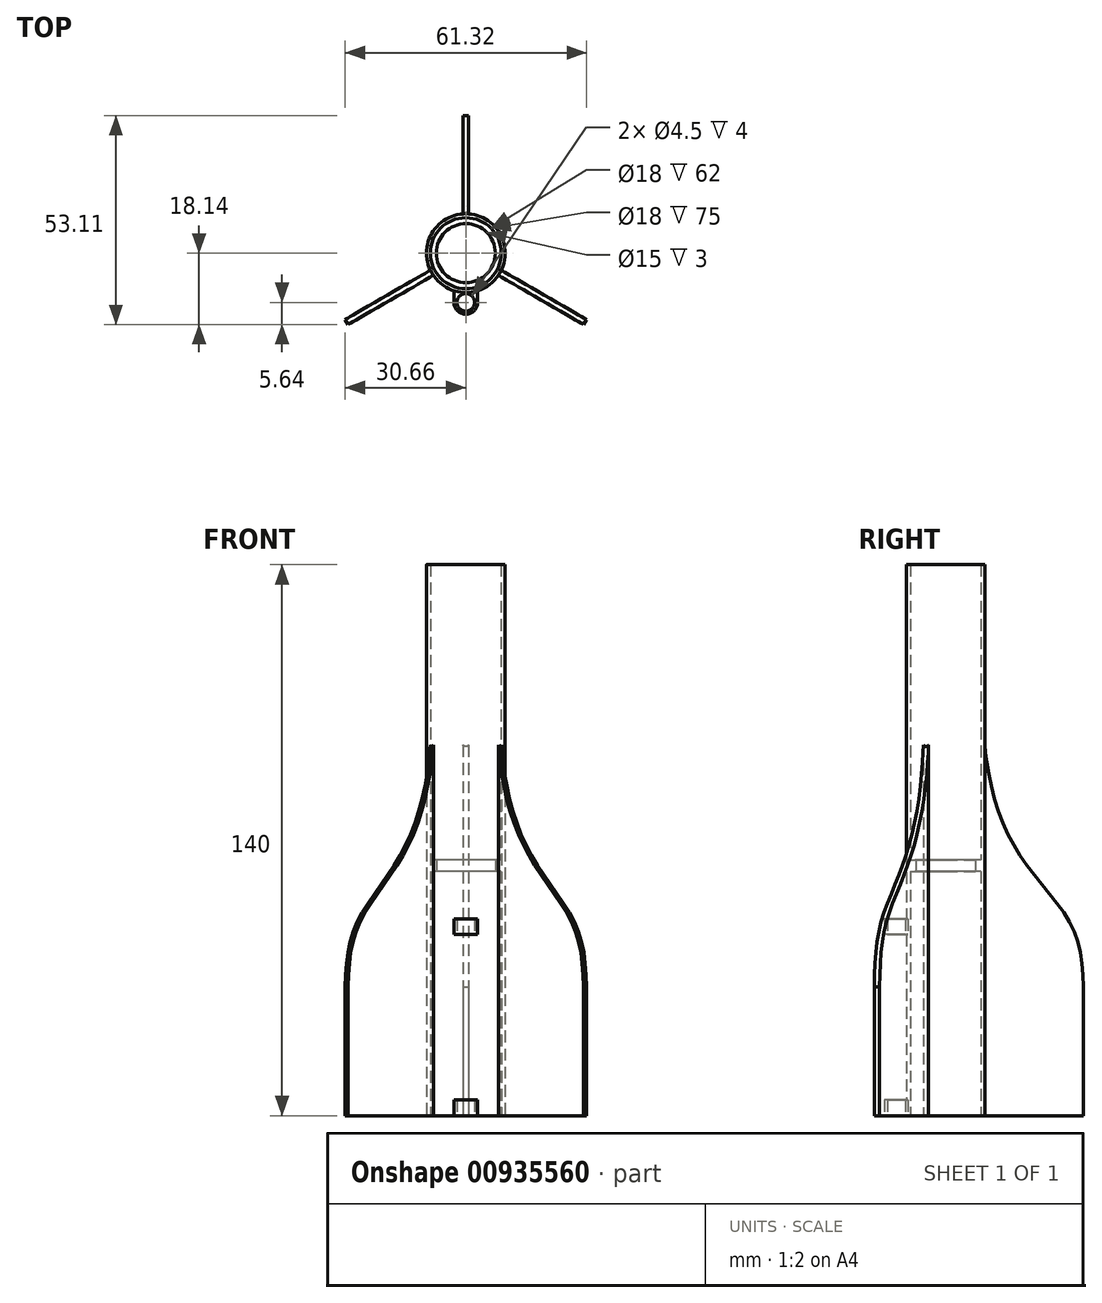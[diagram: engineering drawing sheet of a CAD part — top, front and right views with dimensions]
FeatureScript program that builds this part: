
annotation { "Feature Type Name" : "Feature", "Feature Type Description" : "" }
export const myFeature = defineFeature(function(context is Context, id is Id, definition is map)
    precondition{}
    {
        {
            var Q0;
            Q0=qCreatedBy(makeId("Top.planeOp"),FACE);
            var sketch = newSketch(context, id + "F0", { "sketchPlane" : qUnion([Q0])});
            skCircle(sketch, "E0", {"center": v(0, 0) * mm, "radius": 9 * mm});
            skCircle(sketch, "E1", {"center": v(0, -12.5) * mm, "radius": 2.25 * mm});
            skArc(sketch, "E2", {"start": v(-1.48, -9.89) * mm, "mid": v(0, -15.5) * mm, "end": v(1.48, -9.9) * mm});
            skLineSegment(sketch, "E3", {"start": v(3, -12.5) * mm, "end": v(3, -9.54) * mm});
            skLineSegment(sketch, "E4", {"start": v(-3, -12.5) * mm, "end": v(-3, -9.54) * mm});
            skLineSegment(sketch, "E5.top", {"start": v(0.75, 34.97) * mm, "end": v(-0.75, 34.97) * mm});
            skLineSegment(sketch, "E5.left", {"start": v(0.75, 9.97) * mm, "end": v(0.75, 34.97) * mm});
            skLineSegment(sketch, "E5.right", {"start": v(-0.75, 9.97) * mm, "end": v(-0.75, 34.97) * mm});
            skPoint(sketch, "E5.middle", {"position": v(0, 22.47) * mm});
            skCircle(sketch, "E6", {"center": v(0, 0) * mm, "radius": 10 * mm});
            skCircle(sketch, "E7", {"center": v(0, 0) * mm, "radius": 7.5 * mm});
            skSolve(sketch);
        }
        {
            var Q0;
            Q0=makeQuery(id+"F0.imprint","IMPRINT",FACE,{"disambiguationData":[TD([[makeQuery(id+"F0.imprint","IMPRINT",EDGE,{"derivedFrom":sQuery(id+"F0.wireOp",EDGE,"E0")}),-1.0]])]});
            var Q1;
            {var subQ0=sQuery(id+"F0.wireOp",EDGE,"ZZ5YX0io-akKa-NGHC-uEbq-0SfljBpc04vF");Q1=makeQuery(id+"F0.imprint","IMPRINT",FACE,{"disambiguationData":[TD([[makeQuery(id+"F0.imprint","IMPRINT",EDGE,{"derivedFrom":subQ0}),1.0]])]});}
            extrude(context, id + "F1", {"entities" : qUnion([Q0, Q1]), "depth" : 140 * mm, "offsetDistance" : 25 * mm});
        }
        {
            var Q0;
            Q0=makeQuery(id+"F0.imprint","IMPRINT",FACE,{"disambiguationData":[TD([[makeQuery(id+"F0.imprint","IMPRINT",EDGE,{"derivedFrom":sQuery(id+"F0.wireOp",EDGE,"E5.top")}),1.0]])]});
            extrude(context, id + "F2", {"entities" : qUnion([Q0]), "operationType" : NewBodyOperationType.ADD, "depth" : 100 * mm, "offsetDistance" : 25 * mm});
        }
        {
            var Q0;
            Q0=makeQuery(id+"F2.opExtrude","SWEPT_FACE",FACE,{"disambiguationData":[OSD([sQuery(id+"F0.wireOp",EDGE,"E5.left")])]});
            var sketch = newSketch(context, id + "F3", { "sketchPlane" : qUnion([Q0])});
            skFitSpline(sketch, "E8", {"points": [v(9.97, 100) * mm, v(9.97, 94.16) * mm, v(12.9, 78.8) * mm, v(21.82, 61.99) * mm, v(32.08, 48.03) * mm, v(34.97, 32.7) * mm, v(34.97, 12.12) * mm, v(34.97, 0) * mm], "startDerivative": vector(0, -120.5) * mm, "endDerivative": vector(0, -110.6) * mm});
            skSolve(sketch);
        }
        {
            var Q0;
            {var subQ1=sQuery(id+"F0.wireOp",EDGE,"E5.left");var subQ2=makeQuery(id+"F2.opExtrude","CAP_EDGE",EDGE,{"disambiguationData":[OSD([subQ1])],"isStart":false});Q0=makeQuery(id+"F3.imprint","IMPRINT",FACE,{"disambiguationData":[TD([[makeQuery(id+"F3.imprint","IMPRINT",EDGE,{"derivedFrom":subQ2}),-1.0]])]});}
            extrude(context, id + "F4", {"entities" : qUnion([Q0]), "operationType" : NewBodyOperationType.REMOVE, "endBound" : BoundingType.THROUGH_ALL, "oppositeDirection" : true, "depth" : 25 * mm, "offsetDistance" : 25 * mm});
        }
        {
            var Q0;
            Q0=makeQuery(id+"F1.opExtrude","SWEPT_BODY",BODY,{"disambiguationData":[OSD([sQuery(id+"F0.wireOp",EDGE,"E0"),sQuery(id+"F0.wireOp",EDGE,"lXoG40gP-U72Z-pVJZ-Nn51-esoHy9KuEW7K")])]});
            var Q1;
            Q1=sQuery(id+"F0.wireOp",EDGE,"E0");
            circularPattern(context, id + "F5", {"entities" : qUnion([Q0]), "axis" : qUnion([Q1]), "angle" : 360 * degree, "instanceCount" : 3, "equalSpace" : true, "isCentered" : true});
        }
        {
            var Q0;
            {var subQ0=sQuery(id+"F0.wireOp",EDGE,"E1");Q0=makeQuery(id+"F0.imprint","IMPRINT",FACE,{"disambiguationData":[TD([[makeQuery(id+"F0.imprint","IMPRINT",EDGE,{"derivedFrom":subQ0}),-1.0]])]});}
            var Q1;
            {var subQ3=sQuery(id+"F0.wireOp",EDGE,"E4");Q1=makeQuery(id+"F0.imprint","IMPRINT",FACE,{"disambiguationData":[TD([[makeQuery(id+"F0.imprint","IMPRINT",EDGE,{"derivedFrom":subQ3}),-1.0]])]});}
            var Q2;
            {var subQ3=sQuery(id+"F0.wireOp",EDGE,"E3");Q2=makeQuery(id+"F0.imprint","IMPRINT",FACE,{"disambiguationData":[TD([[makeQuery(id+"F0.imprint","IMPRINT",EDGE,{"derivedFrom":subQ3}),1.0]])]});}
            extrude(context, id + "F6", {"entities" : qUnion([Q0, Q1, Q2]), "operationType" : NewBodyOperationType.ADD, "depth" : 4 * mm, "offsetDistance" : 25 * mm});
        }
        {
            var Q0;
            Q0=makeQuery(id+"F0.imprint","IMPRINT",FACE,{"disambiguationData":[TD([[makeQuery(id+"F0.imprint","IMPRINT",EDGE,{"derivedFrom":sQuery(id+"F0.wireOp",EDGE,"E1")}),-1.0]])]});
            var Q1;
            {var subQ3=sQuery(id+"F0.wireOp",EDGE,"E4");Q1=makeQuery(id+"F0.imprint","IMPRINT",FACE,{"disambiguationData":[TD([[makeQuery(id+"F0.imprint","IMPRINT",EDGE,{"derivedFrom":subQ3}),-1.0]])]});}
            var Q2;
            {var subQ3=sQuery(id+"F0.wireOp",EDGE,"E3");Q2=makeQuery(id+"F0.imprint","IMPRINT",FACE,{"disambiguationData":[TD([[makeQuery(id+"F0.imprint","IMPRINT",EDGE,{"derivedFrom":subQ3}),1.0]])]});}
            extrude(context, id + "F7", {"entities" : qUnion([Q0, Q1, Q2]), "operationType" : NewBodyOperationType.ADD, "depth" : 50 * mm, "offsetDistance" : 25 * mm, "hasSecondDirection" : true, "secondDirectionOppositeDirection" : false, "secondDirectionDepth" : 46 * mm});
        }
        {
            var Q0;
            Q0=makeQuery(id+"F0.imprint","IMPRINT",FACE,{"disambiguationData":[TD([[makeQuery(id+"F0.imprint","IMPRINT",EDGE,{"derivedFrom":sQuery(id+"F0.wireOp",EDGE,"E0")}),1.0]])]});
            extrude(context, id + "F8", {"entities" : qUnion([Q0]), "operationType" : NewBodyOperationType.ADD, "depth" : 65 * mm, "offsetDistance" : 25 * mm, "hasSecondDirection" : true, "secondDirectionOppositeDirection" : false, "secondDirectionDepth" : 62 * mm});
        }
    });
